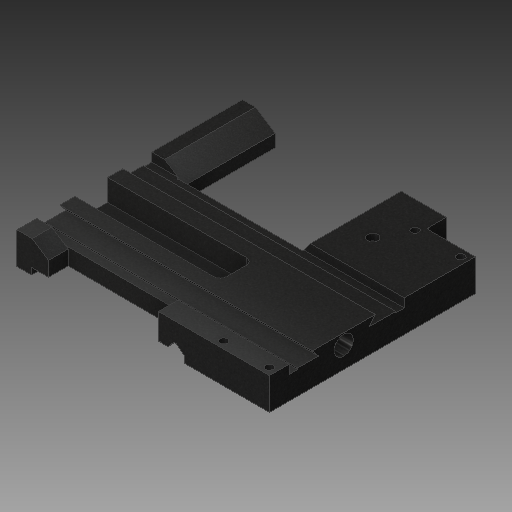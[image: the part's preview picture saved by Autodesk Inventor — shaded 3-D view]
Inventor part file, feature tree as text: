
AUTODESK INVENTOR PART (.ipt)
format: ipt  version: 2018 (Build 220112000, 112)  size: 355,328 bytes
history: native  units: in
note: dims shown in document units (in); Inventor stores cm internally (conversion verified against a paired STEP export)
features: extrude x15, sketch x12
ambient origin geometry x8: Origin, YZ Plane, XZ Plane, XY Plane, X Axis, Y Axis, Z Axis, Center Point
bodies: Solid1 (feature_tree)
feature tree (27):
  extrude  "Extrusion1"  Depth=13.5039in
  extrude  "Extrusion2"  Depth=1.9094in TaperAngle=0.0deg
  extrude  "Extrusion3"  Depth=1.378in
  extrude  "Extrusion4"  Depth=0.8933in
  extrude  "Extrusion8"  Depth=0.0787in
  extrude  "Extrusion19"  Depth=1.1811in
  extrude  "Extrusion20"  Depth=0.1181in
  extrude  "Extrusion21"  Depth=0.3937in
  extrude  "Extrusion22"  Depth=1.2992in
  extrude  "Extrusion23"  Depth=0.4567in
  extrude  "Extrusion24"  TaperAngle=0.0deg  [1 undecoded]
  extrude  "Extrusion25"  Depth=0.0787in TaperAngle=0.0deg
  extrude  "Extrusion26"  Depth=2.2441in
  extrude  "Extrusion27"  Depth=0.3937in TaperAngle=0.0deg
  extrude  "Extrusion28"  Depth=2.2441in
  sketch  "Sketch1"  dims[d0=15.1181in d1=13.5039in]
  sketch  "Sketch12"  dims[d2=1.9094in d3=0.0in d12=1.9094in d13=0.0in]
  sketch  "Sketch28"  dims[d23=1.378in d27=3.7795in]
  sketch  "Sketch29"  dims[d29=1.7323in d32=0.8933in]
  sketch  "Sketch30"  dims[d35=1.9094in d36=0.0in d37=0.0787in]
  sketch  "Sketch32"  dims[d38=0.5118in d43=1.1811in]
  sketch  "Sketch36"  dims[d44=1.9094in d45=0.0in d46=0.1181in]
  sketch  "Sketch37"  dims[d52=0.3436in d72=0.3937in]
  sketch  "Sketch38"  dims[d73=1.2992in d74=0.0in d146=0.4567in]
  sketch  "Sketch40"  dims[d149=0.4567in d152=0.4567in]
  sketch  "Sketch41"  dims[d155=0.4567in d156=0.0in d157=0.0in]
  sketch  "Sketch42"  dims[d159=0.0787in d160=0.0in d161=0.0787in d162=0.0in d168=0.6299in d169=0.3937in d170=0.0in d209=0.6299in d210=45.0deg d211=0.1811in d214=0.5197in d215=45.0deg d216=0.4724in d224=0.8661in d225=0.3937in d227=0.3937in d228=0.0in d229=0.5512in d232=0.748in d233=5.5118in d234=0.0in d235=5.5118in d236=0.0in d240=0.5197in d242=0.1811in d243=0.6299in d245=5.5118in d246=0.0in d247=0.6693in d248=0.3937in d249=0.0in d250=1.1417in d251=2.2441in d252=0.0in]
note: 1 required parameter value undecoded (feature->parameter linkage not recoverable at this tier; creation-order binding heuristic only, values carry confidence <= 0.55)
